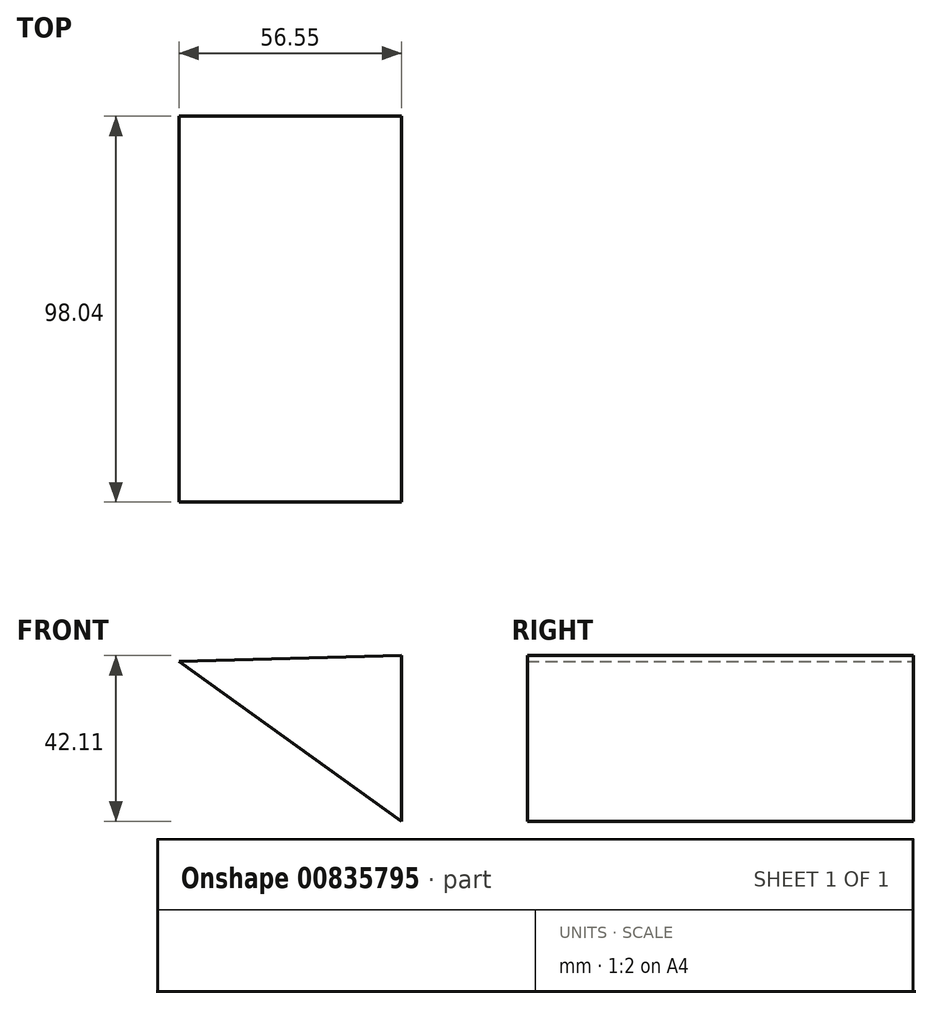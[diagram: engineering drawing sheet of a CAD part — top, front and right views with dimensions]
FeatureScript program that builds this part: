
annotation { "Feature Type Name" : "Feature", "Feature Type Description" : "" }
export const myFeature = defineFeature(function(context is Context, id is Id, definition is map)
    precondition{}
    {
        {
            var Q0;
            Q0=qCreatedBy(makeId("Front.planeOp"),FACE);
            var sketch = newSketch(context, id + "F0", { "sketchPlane" : qUnion([Q0])});
            skLineSegment(sketch, "E0", {"start": v(-35.04, 45.57) * mm, "end": v(21.5, 4.96) * mm});
            skLineSegment(sketch, "E1", {"start": v(21.5, 4.96) * mm, "end": v(21.5, 47.07) * mm});
            skLineSegment(sketch, "E2", {"start": v(21.5, 47.07) * mm, "end": v(-35.04, 45.57) * mm});
            skSolve(sketch);
        }
        {
            var Q0;
            Q0=makeQuery(id+"F0.imprint","IMPRINT",FACE,{"disambiguationData":[TD([[makeQuery(id+"F0.imprint","IMPRINT",EDGE,{"derivedFrom":sQuery(id+"F0.wireOp",EDGE,"E0")}),1.0]])]});
            extrude(context, id + "F1", {"entities" : qUnion([Q0]), "depth" : 98.04 * mm, "offsetDistance" : 25.4 * mm});
        }
    });
